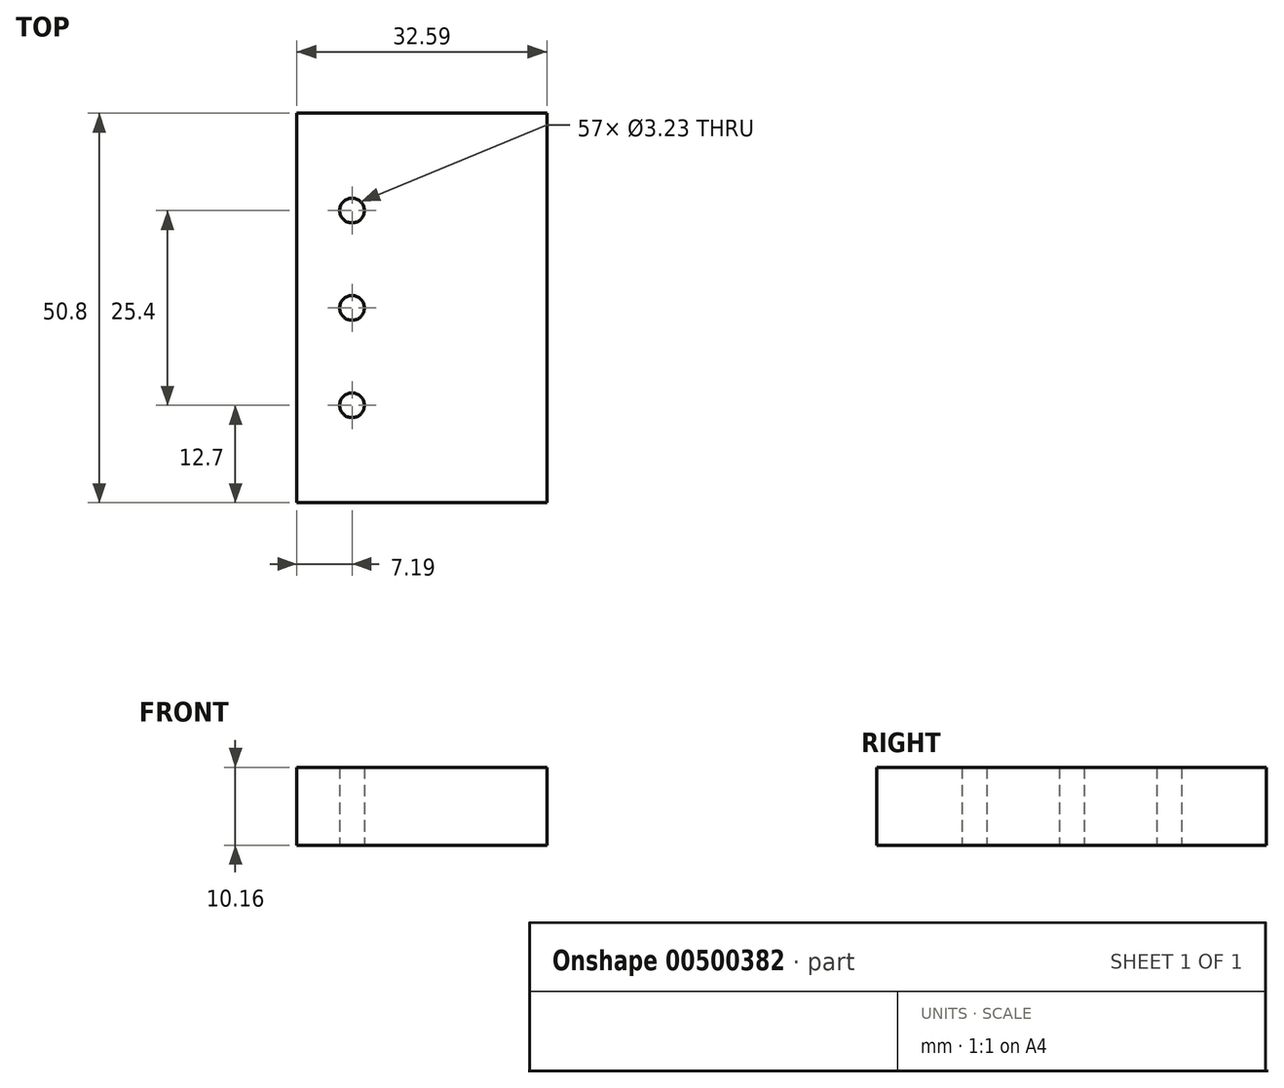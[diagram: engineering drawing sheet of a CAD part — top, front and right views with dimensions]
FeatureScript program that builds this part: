
annotation { "Feature Type Name" : "Feature", "Feature Type Description" : "" }
export const myFeature = defineFeature(function(context is Context, id is Id, definition is map)
    precondition{}
    {
        {
            var Q0;
            Q0=qCreatedBy(makeId("Top.planeOp"),FACE);
            var sketch = newSketch(context, id + "F0", { "sketchPlane" : qUnion([Q0])});
            skLineSegment(sketch, "E0.bottom", {"start": v(18.2, 0) * mm, "end": v(50.8, 0) * mm});
            skLineSegment(sketch, "E0.top", {"start": v(18.2, 50.8) * mm, "end": v(50.8, 50.8) * mm});
            skLineSegment(sketch, "E0.right", {"start": v(50.8, 0) * mm, "end": v(50.8, 50.8) * mm});
            skCircle(sketch, "E1", {"center": v(25.4, 25.4) * mm, "radius": 1.61 * mm});
            skCircle(sketch, "E2", {"center": v(25.4, 12.7) * mm, "radius": 1.61 * mm});
            skCircle(sketch, "E3", {"center": v(25.4, 38.1) * mm, "radius": 1.61 * mm});
            skPoint(sketch, "E4.orphan", {"position": v(38.1, 38.1) * mm});
            skPoint(sketch, "E5.orphan", {"position": v(25.4, 50.8) * mm});
            skPoint(sketch, "E6.orphan", {"position": v(0, 25.4) * mm});
            skPoint(sketch, "E7.end.orphan", {"position": v(38.1, 12.7) * mm});
            skPoint(sketch, "E7.start.orphan", {"position": v(50.8, 25.4) * mm});
            skPoint(sketch, "E8.orphan", {"position": v(25.4, 0) * mm});
            skLineSegment(sketch, "E9", {"start": v(18.2, 0) * mm, "end": v(18.2, 50.8) * mm});
            skPoint(sketch, "E10.orphan", {"position": v(0, 50.8) * mm});
            skPoint(sketch, "E0.left.start.orphan", {"position": v(0, 0) * mm});
            skSolve(sketch);
        }
        {
            var Q0;
            Q0 = qSketchRegion(id + "F0", true);
            extrude(context, id + "F1", {"entities" : qUnion([Q0]), "depth" : 10.16 * mm});
        }
    });
